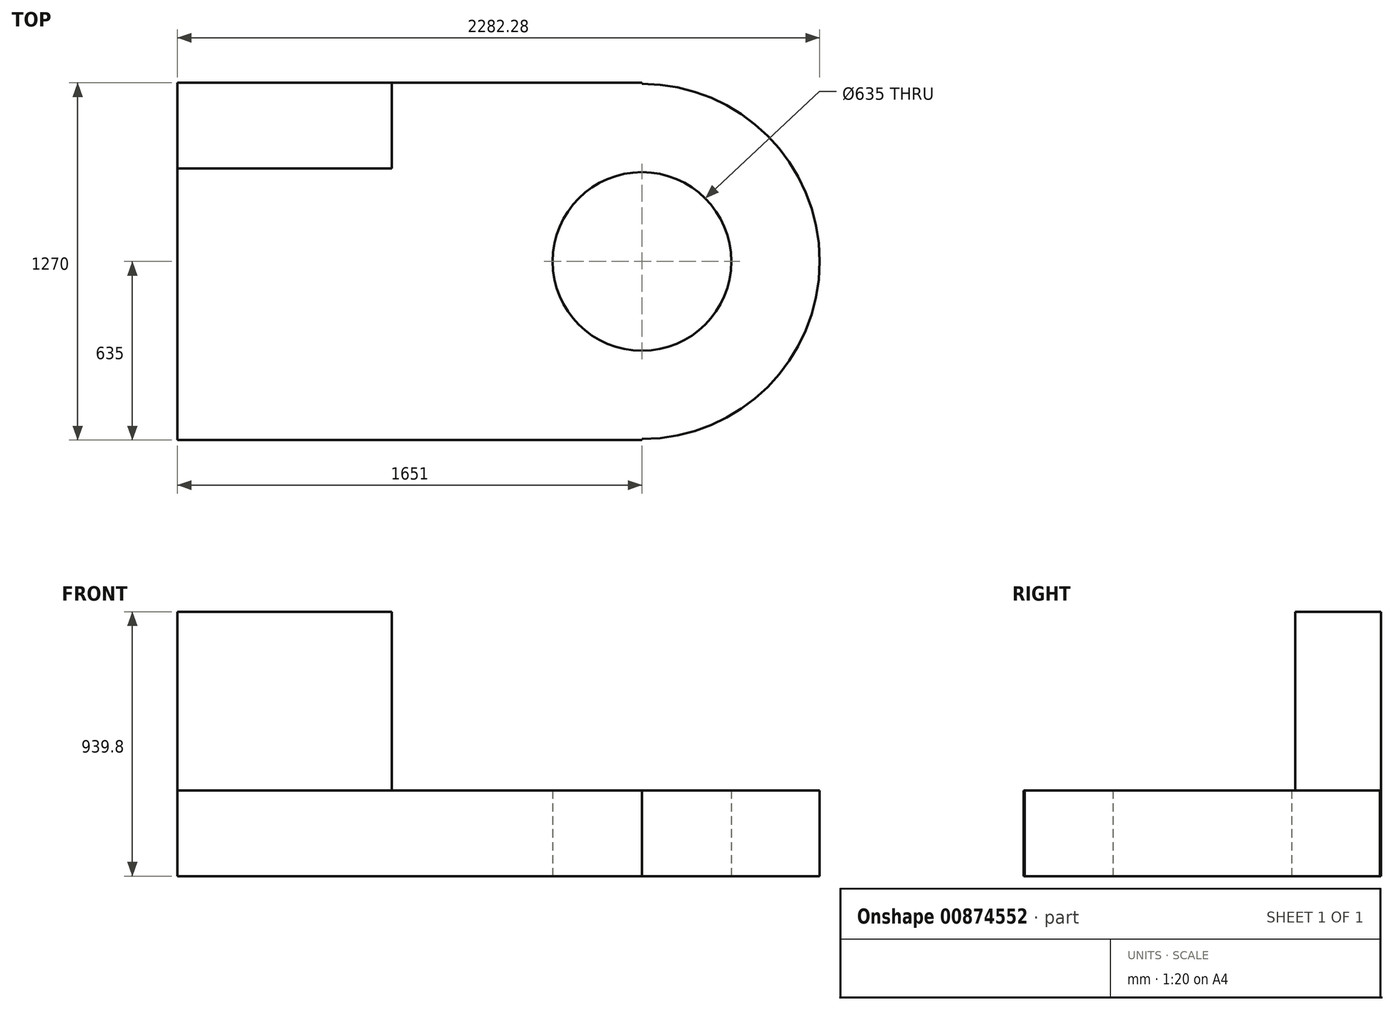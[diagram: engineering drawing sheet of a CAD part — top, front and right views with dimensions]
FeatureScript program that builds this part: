
annotation { "Feature Type Name" : "Feature", "Feature Type Description" : "" }
export const myFeature = defineFeature(function(context is Context, id is Id, definition is map)
    precondition{}
    {
        {
            var Q0;
            Q0=qCreatedBy(makeId("Top.planeOp"),FACE);
            var sketch = newSketch(context, id + "F0", { "sketchPlane" : qUnion([Q0])});
            skLineSegment(sketch, "E0.bottom", {"start": v(0, 0) * mm, "end": v(-1651, 0) * mm});
            skLineSegment(sketch, "E0.top", {"start": v(0, -1270) * mm, "end": v(-1651, -1270) * mm});
            skLineSegment(sketch, "E0.left", {"start": v(0, 0) * mm, "end": v(0, -1270) * mm});
            skLineSegment(sketch, "E0.right", {"start": v(-1651, 0) * mm, "end": v(-1651, -1270) * mm});
            skArc(sketch, "E1", {"start": v(0, -1266.28) * mm, "mid": v(631.28, -635) * mm, "end": v(0, -3.72) * mm});
            skCircle(sketch, "E2", {"center": v(0, -635) * mm, "radius": 317.5 * mm});
            skSolve(sketch);
        }
        {
            var Q0;
            {var subQ5=sQuery(id+"F0.wireOp",EDGE,"E0.bottom");Q0=makeQuery(id+"F0.imprint","IMPRINT",FACE,{"disambiguationData":[TD([[makeQuery(id+"F0.imprint","IMPRINT",EDGE,{"derivedFrom":subQ5}),1.0]])]});}
            var Q1;
            {var subQ0=sQuery(id+"F0.wireOp",EDGE,"E1");Q1=makeQuery(id+"F0.imprint","IMPRINT",FACE,{"disambiguationData":[TD([[makeQuery(id+"F0.imprint","IMPRINT",EDGE,{"derivedFrom":subQ0}),1.0]])]});}
            extrude(context, id + "F1", {"entities" : qUnion([Q0, Q1]), "depth" : 304.8 * mm, "offsetDistance" : 25.4 * mm});
        }
        {
            var Q0;
            Q0=makeQuery(id+"F1.opExtrude","CAP_FACE",FACE,{"disambiguationData":[OSD([sQuery(id+"F0.wireOp",EDGE,"E0.bottom"),sQuery(id+"F0.wireOp",EDGE,"E0.top"),sQuery(id+"F0.wireOp",EDGE,"E0.left"),sQuery(id+"F0.wireOp",EDGE,"E0.right"),sQuery(id+"F0.wireOp",EDGE,"E1"),sQuery(id+"F0.wireOp",EDGE,"E2")])],"isStart":false});
            var sketch = newSketch(context, id + "F2", { "sketchPlane" : qUnion([Q0])});
            skLineSegment(sketch, "E3.bottom", {"start": v(-1651, 0) * mm, "end": v(-889, 0) * mm});
            skLineSegment(sketch, "E3.top", {"start": v(-1651, -304.8) * mm, "end": v(-889, -304.8) * mm});
            skLineSegment(sketch, "E3.left", {"start": v(-1651, 0) * mm, "end": v(-1651, -304.8) * mm});
            skLineSegment(sketch, "E3.right", {"start": v(-889, 0) * mm, "end": v(-889, -304.8) * mm});
            skSolve(sketch);
        }
        {
            var Q0;
            Q0=makeQuery(id+"F2.imprint","IMPRINT",FACE,{"disambiguationData":[TD([[makeQuery(id+"F2.imprint","IMPRINT",EDGE,{"derivedFrom":sQuery(id+"F2.wireOp",EDGE,"E3.bottom")}),1.0]])]});
            extrude(context, id + "F3", {"entities" : qUnion([Q0]), "operationType" : NewBodyOperationType.ADD, "depth" : 635 * mm, "offsetDistance" : 25.4 * mm});
        }
    });
